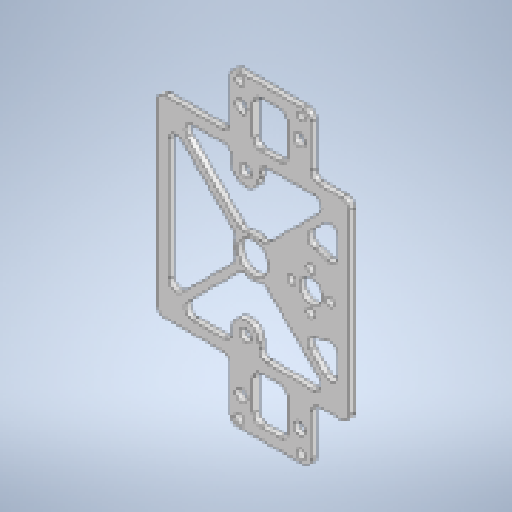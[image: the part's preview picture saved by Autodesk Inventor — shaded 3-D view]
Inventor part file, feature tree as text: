
AUTODESK INVENTOR PART (.ipt)
format: ipt  version: 2025.1 (Build 291241000, 241)  size: 400,896 bytes
history: native  units: mm
features: reference x20, extrude x8, sketch x8, other x6, fillet x4, projected_geometry x2
ambient origin geometry x8: Origin, YZ Plane, XZ Plane, XY Plane, X Axis, Y Axis, Z Axis, Center Point
bodies: Body1 (feature_tree)
feature tree (48):
  other  "ソリッド1"
  extrude  "押し出し1"  Depth=1.5mm TaperAngle=0.0deg
  extrude  "押し出し2"  Depth=10.0mm TaperAngle=0.0deg
  fillet  "フィレット2"  Radius=2.0mm
  extrude  "押し出し3"  Depth=20.0mm
  extrude  "押し出し4"  Depth=10.0mm
  extrude  "押し出し5"  Depth=2.2mm
  extrude  "押し出し6"  Depth=40.0mm TaperAngle=360.0deg
  fillet  "フィレット3"  [1 undecoded]
  extrude  "押し出し7"  TaperAngle=0.0deg  [1 undecoded]
  fillet  "フィレット4"  [1 undecoded]
  extrude  "押し出し8"  Depth=3.0mm
  fillet  "フィレット5"  Radius=8.0mm
  sketch  "スケッチ1"
  reference  "参照1"
  sketch  "スケッチ3"
  projected_geometry  "投影ループ2"
  reference  "参照2"
  reference  "参照3"
  reference  "参照4"
  reference  "参照5"
  reference  "参照6"
  reference  "参照7"
  reference  "参照8"
  reference  "参照9"
  reference  "参照10"
  reference  "参照11"
  reference  "参照12"
  reference  "参照13"
  reference  "参照14"
  reference  "参照15"
  sketch  "スケッチ4"
  other  "スケッチ円形状パターン1"
  sketch  "スケッチ5"
  reference  "参照16"
  reference  "参照17"
  reference  "参照18"
  reference  "参照19"
  sketch  "スケッチ6"
  reference  "参照20"
  sketch  "スケッチ7"
  projected_geometry  "投影ループ3"
  sketch  "スケッチ8"
  sketch  "スケッチ9"
  other  "<userpath>\Documents\Inventor\Vixen\doutai.iam"
  other  "doutai.iam"
  other  "katasita:1"
  other  "fox:1"
note: 3 required parameter values undecoded (feature->parameter linkage not recoverable at this tier; creation-order binding heuristic only, values carry confidence <= 0.55)
